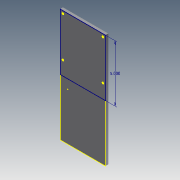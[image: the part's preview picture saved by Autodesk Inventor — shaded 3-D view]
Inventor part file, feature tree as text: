
AUTODESK INVENTOR PART (.ipt)
format: ipt  version: 2011 (Build 150239000, 239)  size: 161,792 bytes
history: native  units: in
note: dims shown in document units (in); Inventor stores cm internally (conversion verified against a paired STEP export)
features: extrude x5, sketch x5
ambient origin geometry x8: Origin, YZ Plane, XZ Plane, XY Plane, X Axis, Y Axis, Z Axis, Center Point
bodies: Solid1 (feature_tree)
feature tree (10):
  extrude  "Extrusion1"  Depth=10.0in
  extrude  "Extrusion2"  Depth=0.235in
  extrude  "Extrusion3"  Depth=3.53in
  extrude  "Extrusion4"  Depth=0.25in TaperAngle=0.0deg
  extrude  "Extrusion5"  Depth=5.0in
  sketch  "Sketch1"  dims[d0=4.0in d1=10.0in]
  sketch  "Sketch2"  dims[d2=0.235in d3=0.235in]
  sketch  "Sketch3"  dims[d4=0.235in d5=3.53in]
  sketch  "Sketch4"  dims[d6=0.156in d7=0.25in d8=0.0in]
  sketch  "Sketch5"  dims[d9=1.0in d10=0.0in d11=5.0in d12=1.0in d13=0.0in d14=0.9055in d15=0.4134in d16=0.8268in d17=1.378in d18=1.0in d19=0.0in d20=0.5315in d21=0.2559in d22=1.063in d23=0.6299in d24=0.0787in d25=1.0in d26=0.0in]
